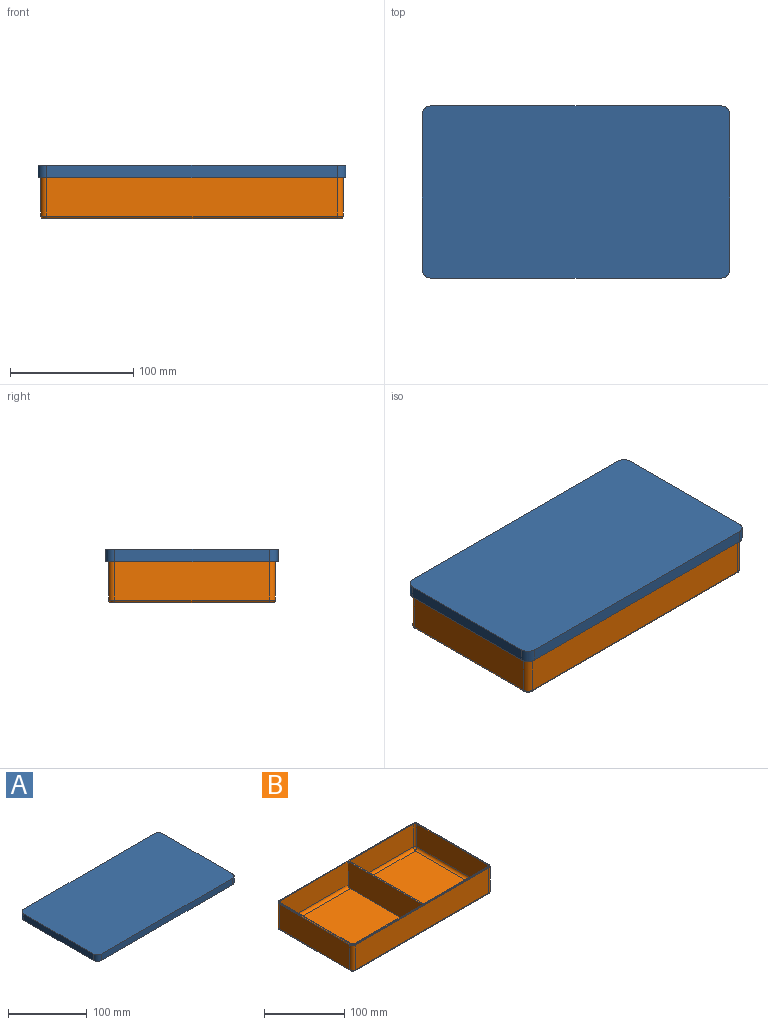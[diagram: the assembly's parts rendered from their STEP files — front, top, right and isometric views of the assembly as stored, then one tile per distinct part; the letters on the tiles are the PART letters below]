
ASSEMBLY  parts=2 mates=1
PART A: 27 faces, bbox 250x140x10 mm
  f0: plane 125x10mm, normal (-1,0,0), area 1250mm2, adj f1,f15,f16,f17
  f1: cylinder r=7.2mm len=10mm, axis (0,0,1), area 113.1mm2, adj f0,f2,f16,f17
  f2: plane 235x10mm, normal (0,-1,0), area 2350mm2, adj f1,f3,f16,f17
  f3: cylinder r=7.2mm len=10mm, axis (0,0,1), area 113.1mm2, adj f2,f4,f16,f17
  f4: plane 125x10mm, normal (1,0,0), area 1250mm2, adj f3,f5,f16,f17
  f5: cylinder r=7.2mm len=10mm, axis (0,0,1), area 113.1mm2, adj f4,f6,f16,f17
  f6: plane 235x10mm, normal (0,1,0), area 2350mm2, adj f5,f15,f16,f17
  f7: cylinder r=5.2mm len=7mm, axis (0,0,1), area 57.2mm2, adj f8,f14,f18,f21
  f8: plane 235x7mm, normal (0,-1,0), area 1645mm2, adj f7,f9,f18,f23
  f9: cylinder r=5.2mm len=7mm, axis (0,0,1), area 57.2mm2, adj f8,f10,f18,f25
  f10: plane 125x7mm, normal (-1,0,0), area 875mm2, adj f9,f11,f18,f26
  f11: cylinder r=5.2mm len=7mm, axis (0,0,1), area 57.2mm2, adj f10,f12,f18,f24
  f12: plane 235x7mm, normal (0,1,0), area 1645mm2, adj f11,f13,f18,f22
  f13: cylinder r=5.2mm len=7mm, axis (0,0,1), area 57.2mm2, adj f12,f14,f18,f20
  f14: plane 125x7mm, normal (1,0,0), area 875mm2, adj f7,f13,f18,f19
  f15: cylinder r=7.2mm len=10mm, axis (0,0,1), area 113.1mm2, adj f0,f6,f16,f17
  f16: plane 249.4x139.4mm, normal (0,0,-1), area 762.1mm2, adj f0,f1,f2,f3,f4,f5,f6,f15
  f17: plane 249.4x139.4mm, normal (0,0,1), area 34721.9mm2, adj f0,f1,f2,f3,f4,f5,f6,f15
  f18: plane 245.4x135.4mm, normal (0,0,-1), area 33203.9mm2, adj f7,f8,f9,f10,f11,f12,f13,f14
  f19: cylinder r=1mm len=125mm, axis (0,-1,0), area 196.3mm2, adj f14,f16,f20,f21
  f20: torus R=6.2mm, axis (0,0,1), area 13.7mm2, adj f13,f16,f19,f22
  f21: torus R=6.2mm, axis (0,0,1), area 13.7mm2, adj f7,f16,f19,f23
  f22: cylinder r=1mm len=235mm, axis (1,0,0), area 369.1mm2, adj f12,f16,f20,f24
  f23: cylinder r=1mm len=235mm, axis (-1,0,0), area 369.1mm2, adj f8,f16,f21,f25
  f24: torus R=6.2mm, axis (0,0,1), area 13.7mm2, adj f11,f16,f22,f26
  f25: torus R=6.2mm, axis (0,0,1), area 13.7mm2, adj f9,f16,f23,f26
  f26: cylinder r=1mm len=125mm, axis (0,1,0), area 196.3mm2, adj f10,f16,f24,f25
PART B: 50 faces, bbox 245.8x135.8x41 mm
  f0: plane 125x38mm, normal (1,0,0), area 4750mm2, adj f1,f7,f24,f42
  f1: cylinder r=5mm len=38mm, axis (0,0,-1), area 298.5mm2, adj f0,f2,f26,f44
  f2: plane 235x38mm, normal (0,1,0), area 8930mm2, adj f1,f3,f28,f46
  f3: cylinder r=5mm len=38mm, axis (0,0,-1), area 298.5mm2, adj f2,f4,f30,f48
  f4: plane 125x38mm, normal (-1,0,0), area 4750mm2, adj f3,f5,f31,f49
  f5: cylinder r=5mm len=38mm, axis (0,0,-1), area 298.5mm2, adj f4,f6,f29,f47
  f6: plane 235x38mm, normal (0,-1,0), area 8930mm2, adj f5,f7,f27,f45
  f7: cylinder r=5mm len=38mm, axis (0,0,-1), area 298.5mm2, adj f0,f6,f25,f43
  f8: plane 241x131mm, normal (0,0,-1), area 31563.3mm2, adj f42,f43,f44,f45,f46,f47,f48,f49
  f9: plane 119.5x35mm, normal (0,-1,0), area 4182.5mm2, adj f10,f19,f21,f36
  f10: plane 131x39mm, normal (-1,0,0), area 5102.1mm2, adj f9,f11,f21,f23,f32,f36
  f11: plane 119.5x35mm, normal (0,1,0), area 4182.5mm2, adj f10,f12,f21,f32
  f12: cylinder r=3mm len=35mm, axis (0,0,-1), area 164.9mm2, adj f11,f13,f21,f33
  f13: plane 125x35mm, normal (1,0,0), area 4375mm2, adj f12,f19,f21,f34
  f14: plane 131x39mm, normal (1,0,0), area 5102.1mm2, adj f15,f20,f21,f22,f37,f41
  f15: plane 113.5x35mm, normal (0,-1,0), area 3972.5mm2, adj f14,f16,f21,f41
  f16: cylinder r=3mm len=35mm, axis (0,0,-1), area 164.9mm2, adj f15,f17,f21,f40
  f17: plane 125x35mm, normal (-1,0,0), area 4375mm2, adj f16,f18,f21,f39
  f18: cylinder r=3mm len=35mm, axis (0,0,-1), area 164.9mm2, adj f17,f20,f21,f38
  f19: cylinder r=3mm len=35mm, axis (0,0,-1), area 164.9mm2, adj f9,f13,f21,f35
  f20: plane 113.5x35mm, normal (0,1,0), area 3972.5mm2, adj f14,f18,f21,f37
  f21: plane 243x133mm, normal (0,0,1), area 1004mm2, adj f9,f10,f11,f12,f13,f14,f15,f16
  f22: plane 123x112.5mm, normal (0,0,1), area 13837.5mm2, adj f14,f37,f39,f41
  f23: plane 123x118.5mm, normal (0,0,1), area 14575.5mm2, adj f10,f32,f34,f36
  f24: cylinder r=1mm len=125mm, axis (0,-1,0), area 196.3mm2, adj f0,f21,f25,f26
  f25: torus R=4mm, axis (0,0,1), area 11.4mm2, adj f7,f21,f24,f27
  f26: torus R=4mm, axis (0,0,1), area 11.4mm2, adj f1,f21,f24,f28
  f27: cylinder r=1mm len=235mm, axis (-1,0,0), area 369.1mm2, adj f6,f21,f25,f29
  f28: cylinder r=1mm len=235mm, axis (1,0,0), area 369.1mm2, adj f2,f21,f26,f30
  f29: torus R=4mm, axis (0,0,1), area 11.4mm2, adj f5,f21,f27,f31
  f30: torus R=4mm, axis (0,0,1), area 11.4mm2, adj f3,f21,f28,f31
  f31: cylinder r=1mm len=125mm, axis (0,1,0), area 196.3mm2, adj f4,f21,f29,f30
  f32: cylinder r=4mm len=119.5mm, axis (1,0,0), area 748.6mm2, adj f10,f11,f23,f33
  f33: bspline ~4.9x4mm, area 19.3mm2, adj f12,f32,f34
  f34: cylinder r=4mm len=125mm, axis (0,-1,0), area 780.8mm2, adj f13,f23,f33,f35
  f35: bspline ~4.9x4mm, area 19.3mm2, adj f19,f34,f36
  f36: cylinder r=4mm len=119.5mm, axis (-1,0,0), area 748.6mm2, adj f9,f10,f23,f35
  f37: cylinder r=4mm len=113.5mm, axis (1,0,0), area 710.9mm2, adj f14,f20,f22,f38
  f38: bspline ~4.9x4mm, area 19.3mm2, adj f18,f37,f39
  f39: cylinder r=4mm len=125mm, axis (0,1,0), area 780.8mm2, adj f17,f22,f38,f40
  f40: bspline ~4.9x4mm, area 19.3mm2, adj f16,f39,f41
  f41: cylinder r=4mm len=113.5mm, axis (-1,0,0), area 710.9mm2, adj f14,f15,f22,f40
  f42: cylinder r=2mm len=125mm, axis (0,1,0), area 392.7mm2, adj f0,f8,f43,f44
  f43: torus R=3mm, axis (0,0,1), area 21.1mm2, adj f7,f8,f42,f45
  f44: torus R=3mm, axis (0,0,1), area 21.1mm2, adj f1,f8,f42,f46
  f45: cylinder r=2mm len=235mm, axis (1,0,0), area 738.3mm2, adj f6,f8,f43,f47
  f46: cylinder r=2mm len=235mm, axis (-1,0,0), area 738.3mm2, adj f2,f8,f44,f48
  f47: torus R=3mm, axis (0,0,1), area 21.1mm2, adj f5,f8,f45,f49
  f48: torus R=3mm, axis (0,0,1), area 21.1mm2, adj f3,f8,f46,f49
  f49: cylinder r=2mm len=125mm, axis (0,-1,0), area 392.7mm2, adj f4,f8,f47,f48
PLACE A t=(0,0,-0.5)mm
PLACE B t=(100,0,-43.5)mm
MATE planar B.f21 <-> A.f18  axis (0,0,1) through (223.28,67.5,-2.5)mm
